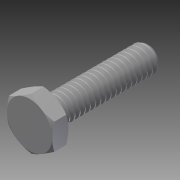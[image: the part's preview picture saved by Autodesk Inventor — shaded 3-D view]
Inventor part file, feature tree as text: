
AUTODESK INVENTOR PART (.ipt)
format: ipt  version: 2014 SP1 (Build 180222100, 222)  size: 640,512 bytes
history: native  units: in
note: dims shown in document units (in); Inventor stores cm internally (conversion verified against a paired STEP export)
features: extrude x1, other x1, imported_body x1
ambient origin geometry x8: Origin, YZ Plane, XZ Plane, XY Plane, X Axis, Y Axis, Z Axis, Center Point
bodies: Body1 (feature_tree)
feature tree (3):
  extrude  "Extrude14"  [1 undecoded]
  other  "92620A5421"
  imported_body  "Base1"
note: 1 required parameter value undecoded (feature->parameter linkage not recoverable at this tier; creation-order binding heuristic only, values carry confidence <= 0.55)
